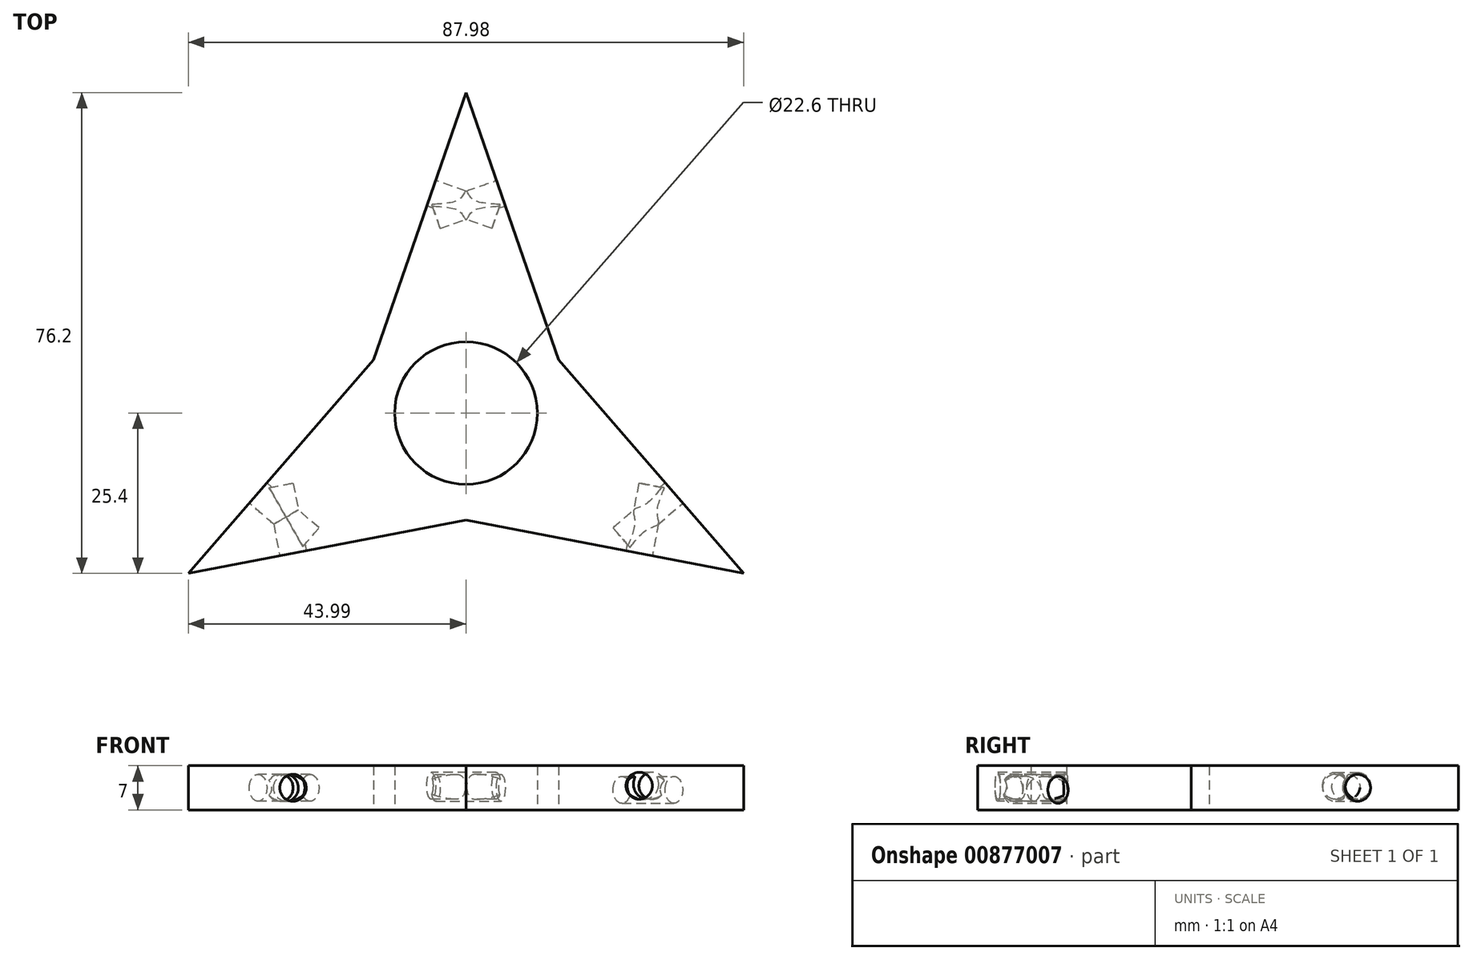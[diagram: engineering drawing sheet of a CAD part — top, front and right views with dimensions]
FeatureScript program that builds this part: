
annotation { "Feature Type Name" : "Feature", "Feature Type Description" : "" }
export const myFeature = defineFeature(function(context is Context, id is Id, definition is map)
    precondition{}
    {
        {
            var Q0;
            Q0=qCreatedBy(makeId("Top.planeOp"),FACE);
            var sketch = newSketch(context, id + "F0", { "sketchPlane" : qUnion([Q0])});
            skLineSegment(sketch, "E0", {"start": v(0, 76.2) * mm, "end": v(14.66, 33.87) * mm});
            skLineSegment(sketch, "E1", {"start": v(14.66, 33.87) * mm, "end": v(44, 0) * mm});
            skLineSegment(sketch, "E2", {"start": v(0, 76.2) * mm, "end": v(-14.66, 33.87) * mm});
            skLineSegment(sketch, "E3", {"start": v(-14.66, 33.87) * mm, "end": v(-44, 0) * mm});
            skLineSegment(sketch, "E4", {"start": v(-44, 0) * mm, "end": v(0, 8.47) * mm});
            skLineSegment(sketch, "E5", {"start": v(0, 8.47) * mm, "end": v(44, 0) * mm});
            skCircle(sketch, "E6", {"center": v(0, 25.4) * mm, "radius": 11.3 * mm});
            skSolve(sketch);
        }
        {
            var Q0;
            Q0 = qSketchRegion(id + "F0", true);
            extrude(context, id + "F1", {"entities" : qUnion([Q0]), "depth" : 7 * mm, "offsetDistance" : 25.4 * mm});
        }
        {
            var Q0;
            Q0=makeQuery(id+"F1.opExtrude","SWEPT_FACE",FACE,{"disambiguationData":[OSD([sQuery(id+"F0.wireOp",EDGE,"E4")])]});
            var sketch = newSketch(context, id + "F2", { "sketchPlane" : qUnion([Q0])});
            skCircle(sketch, "E7", {"center": v(-26.34, 3.5) * mm, "radius": 2.13 * mm});
            skSolve(sketch);
        }
        {
            var Q0;
            Q0=makeQuery(id+"F2.imprint","IMPRINT",FACE,{"disambiguationData":[TD([[makeQuery(id+"F2.imprint","IMPRINT",EDGE,{"derivedFrom":sQuery(id+"F2.wireOp",EDGE,"E7")}),1.0]])]});
            extrude(context, id + "F3", {"entities" : qUnion([Q0]), "operationType" : NewBodyOperationType.REMOVE, "oppositeDirection" : true, "depth" : 10.92 * mm, "offsetDistance" : 25.4 * mm, "hasSecondDirection" : true, "secondDirectionOppositeDirection" : false, "secondDirectionDepth" : 25.4 * mm});
        }
        {
            var Q0;
            Q0=makeQuery(id+"F1.opExtrude","SWEPT_FACE",FACE,{"disambiguationData":[OSD([sQuery(id+"F0.wireOp",EDGE,"E3")])]});
            var sketch = newSketch(context, id + "F4", { "sketchPlane" : qUnion([Q0])});
            skCircle(sketch, "E8", {"center": v(11.94, 3.5) * mm, "radius": 2.13 * mm});
            skSolve(sketch);
        }
        {
            var Q0;
            Q0 = qSketchRegion(id + "F4", true);
            extrude(context, id + "F5", {"entities" : qUnion([Q0]), "operationType" : NewBodyOperationType.REMOVE, "oppositeDirection" : true, "depth" : 10.92 * mm, "offsetDistance" : 25.4 * mm});
        }
        {
            var Q0;
            Q0=makeQuery(id+"F1.opExtrude","SWEPT_FACE",FACE,{"disambiguationData":[OSD([sQuery(id+"F0.wireOp",EDGE,"E0")])]});
            var sketch = newSketch(context, id + "F6", { "sketchPlane" : qUnion([Q0])});
            skCircle(sketch, "E9", {"center": v(55.14, 3.5) * mm, "radius": 2.13 * mm});
            skPoint(sketch, "E10", {"position": v(72, 3.5) * mm});
            skSolve(sketch);
        }
        {
            var Q0;
            Q0 = qSketchRegion(id + "F6", true);
            extrude(context, id + "F7", {"entities" : qUnion([Q0]), "operationType" : NewBodyOperationType.REMOVE, "oppositeDirection" : true, "depth" : 10.92 * mm, "offsetDistance" : 25.4 * mm});
        }
        {
            var Q0;
            Q0=makeQuery(id+"F1.opExtrude","SWEPT_FACE",FACE,{"disambiguationData":[OSD([sQuery(id+"F0.wireOp",EDGE,"E2")])]});
            var sketch = newSketch(context, id + "F8", { "sketchPlane" : qUnion([Q0])});
            skCircle(sketch, "E11", {"center": v(-55.14, 3.83) * mm, "radius": 2.13 * mm});
            skSolve(sketch);
        }
        {
            var Q0;
            Q0 = qSketchRegion(id + "F8", true);
            extrude(context, id + "F9", {"entities" : qUnion([Q0]), "operationType" : NewBodyOperationType.REMOVE, "oppositeDirection" : true, "depth" : 10.92 * mm, "offsetDistance" : 25.4 * mm});
        }
        {
            var Q0;
            Q0=makeQuery(id+"F1.opExtrude","SWEPT_FACE",FACE,{"disambiguationData":[OSD([sQuery(id+"F0.wireOp",EDGE,"E1")])]});
            var sketch = newSketch(context, id + "F10", { "sketchPlane" : qUnion([Q0])});
            skCircle(sketch, "E12", {"center": v(-11.94, 3.18) * mm, "radius": 2.13 * mm});
            skSolve(sketch);
        }
        {
            var Q0;
            Q0=makeQuery(id+"F10.imprint","IMPRINT",FACE,{"disambiguationData":[TD([[makeQuery(id+"F10.imprint","IMPRINT",EDGE,{"derivedFrom":sQuery(id+"F10.wireOp",EDGE,"E12")}),1.0]])]});
            extrude(context, id + "F11", {"entities" : qUnion([Q0]), "operationType" : NewBodyOperationType.REMOVE, "oppositeDirection" : true, "depth" : 10.92 * mm, "offsetDistance" : 25.4 * mm});
        }
        {
            var Q0;
            Q0=makeQuery(id+"F1.opExtrude","SWEPT_FACE",FACE,{"disambiguationData":[OSD([sQuery(id+"F0.wireOp",EDGE,"E5")])]});
            var sketch = newSketch(context, id + "F12", { "sketchPlane" : qUnion([Q0])});
            skCircle(sketch, "E13", {"center": v(26.34, 3.83) * mm, "radius": 2.13 * mm});
            skSolve(sketch);
        }
        {
            var Q0;
            Q0=makeQuery(id+"F12.imprint","IMPRINT",FACE,{"disambiguationData":[TD([[makeQuery(id+"F12.imprint","IMPRINT",EDGE,{"derivedFrom":sQuery(id+"F12.wireOp",EDGE,"E13")}),1.0]])]});
            extrude(context, id + "F13", {"entities" : qUnion([Q0]), "operationType" : NewBodyOperationType.REMOVE, "oppositeDirection" : true, "depth" : 10.92 * mm, "offsetDistance" : 25.4 * mm});
        }
    });
